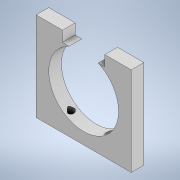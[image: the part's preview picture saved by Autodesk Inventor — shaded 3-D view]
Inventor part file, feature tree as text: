
AUTODESK INVENTOR PART (.ipt)
format: ipt  version: 2022 (Build 260153000, 153)  size: 139,776 bytes
history: native  units: mm
features: sketch x4, extrude x3, hole x1
ambient origin geometry x8: Origin, YZ Plane, XZ Plane, XY Plane, X Axis, Y Axis, Z Axis, Center Point
bodies: Solid1 (feature_tree)
feature tree (8):
  extrude  "Extrusion1"  Depth=45.0mm
  extrude  "Extrusion2"  Depth=10.0mm
  hole  "Hole1"  [1 undecoded]
  extrude  "Extrusion3"  Depth=10.0mm
  sketch  "Sketch1"  dims[d0=45.0mm d1=6.0mm]
  sketch  "Sketch2"  dims[d2=42.0mm d3=0.0mm d4=10.0mm]
  sketch  "Sketch3"  dims[d5=10.0mm d6=5.0mm]
  sketch  "Sketch4"  dims[d7=42.0mm d8=0.0mm d9=3.0mm d10=10.0mm d11=10.0mm d12=4.5mm d13=6.0mm d14=5.0mm d15=2.0mm d16=90.0deg d17=8.0mm d18=20.594885mm d19=22.0mm d20=33.0mm d21=0.0mm d22=0.0mm]
note: 1 required parameter value undecoded (feature->parameter linkage not recoverable at this tier; creation-order binding heuristic only, values carry confidence <= 0.55)
